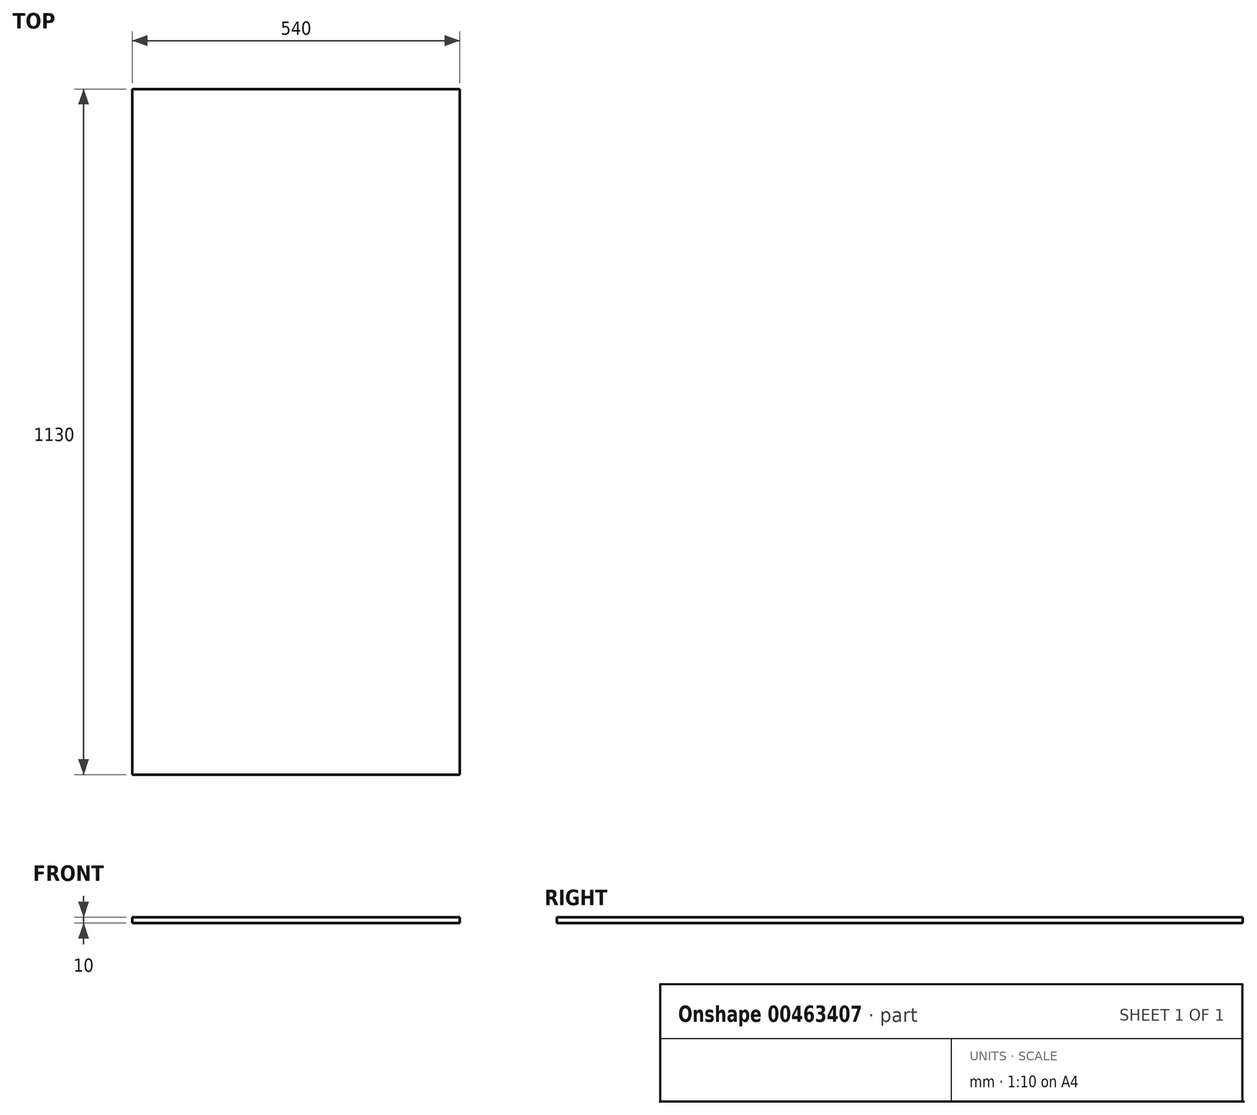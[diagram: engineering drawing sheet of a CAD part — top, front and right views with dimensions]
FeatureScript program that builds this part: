
annotation { "Feature Type Name" : "Feature", "Feature Type Description" : "" }
export const myFeature = defineFeature(function(context is Context, id is Id, definition is map)
    precondition{}
    {
        {
            var Q0;
            Q0=qCreatedBy(makeId("Front.planeOp"),FACE);
            var sketch = newSketch(context, id + "F0", { "sketchPlane" : qUnion([Q0])});
            skLineSegment(sketch, "E0.bottom", {"start": v(-275.66, -62.4) * mm, "end": v(264.34, -62.4) * mm});
            skLineSegment(sketch, "E0.top", {"start": v(-275.66, -72.4) * mm, "end": v(264.34, -72.4) * mm});
            skLineSegment(sketch, "E0.left", {"start": v(-275.66, -62.4) * mm, "end": v(-275.66, -72.4) * mm});
            skLineSegment(sketch, "E0.right", {"start": v(264.34, -62.4) * mm, "end": v(264.34, -72.4) * mm});
            skSolve(sketch);
        }
        {
            var Q0;
            Q0=makeQuery(id+"F0.imprint","IMPRINT",FACE,{"disambiguationData":[TD([[makeQuery(id+"F0.imprint","IMPRINT",EDGE,{"derivedFrom":sQuery(id+"F0.wireOp",EDGE,"E0.bottom")}),-1.0]])]});
            extrude(context, id + "F1", {"entities" : qUnion([Q0]), "oppositeDirection" : true, "depth" : 1130 * mm});
        }
    });
